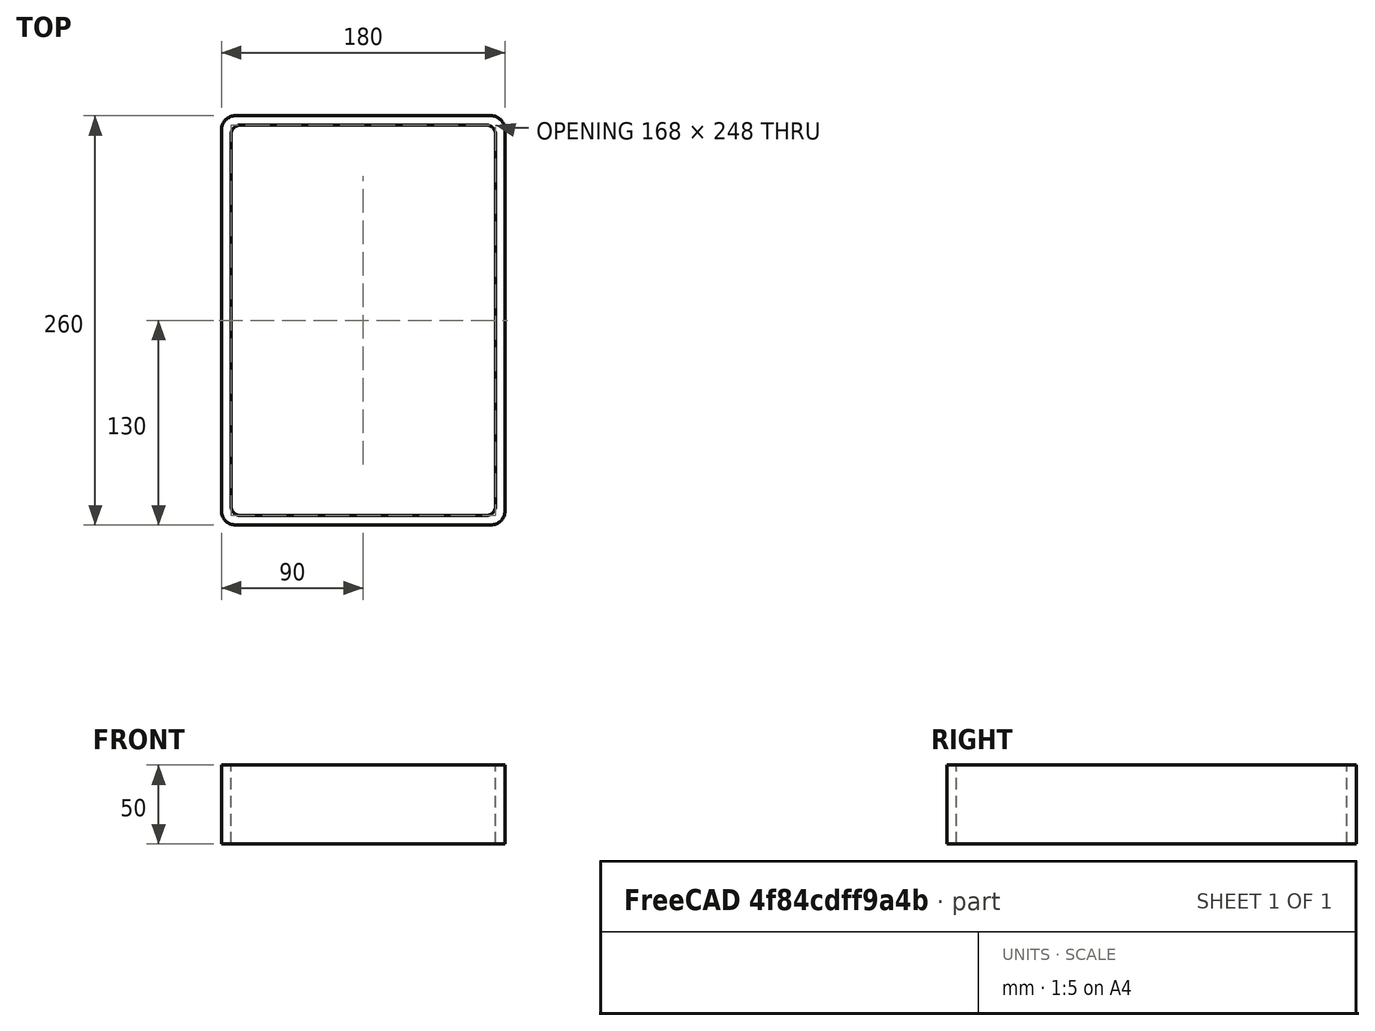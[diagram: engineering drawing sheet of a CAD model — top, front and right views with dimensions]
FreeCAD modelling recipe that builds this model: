
FCSTD DOCUMENT  (FreeCAD 0.15R4671 (Git))
Label: Rectangular hollow section 260x180x6 EN10219 S235JRH
License: All rights reserved
LicenseURL: http://en.wikipedia.org/wiki/All_rights_reserved
objects: Sketcher::SketchObject×1, Part::Extrusion×1
note: 2 computed .brp shape members not serialized (recipe doc carries the construction recipe); baked Part::Feature solids carry a one-line shape summary decoded from their .brp

FEATURE [Sketcher::SketchObject] Sketch
  sketch-geometry (16):
    g0: LineSegment StartX=-78 StartY=124 StartZ=0 EndX=78 EndY=124 EndZ=0
    g1: LineSegment StartX=84 StartY=118 StartZ=0 EndX=84 EndY=-118 EndZ=0
    g2: LineSegment StartX=78 StartY=-124 StartZ=0 EndX=-78 EndY=-124 EndZ=0
    g3: LineSegment StartX=-84 StartY=-118 StartZ=0 EndX=-84 EndY=118 EndZ=0
    g4: LineSegment StartX=-81 StartY=130 StartZ=0 EndX=81 EndY=130 EndZ=0
    g5: LineSegment StartX=90 StartY=121 StartZ=0 EndX=90 EndY=-121 EndZ=0
    g6: LineSegment StartX=81 StartY=-130 StartZ=0 EndX=-81 EndY=-130 EndZ=0
    g7: LineSegment StartX=-90 StartY=-121 StartZ=0 EndX=-90 EndY=121 EndZ=0
    g8: ArcOfCircle CenterX=-78 CenterY=118 CenterZ=0 NormalX=0 NormalY=0 NormalZ=1 Radius=6 StartAngle=1.5708 EndAngle=3.14159
    g9: ArcOfCircle CenterX=78 CenterY=118 CenterZ=0 NormalX=0 NormalY=0 NormalZ=1 Radius=6 StartAngle=0 EndAngle=1.5708
    g10: ArcOfCircle CenterX=78 CenterY=-118 CenterZ=0 NormalX=0 NormalY=0 NormalZ=1 Radius=6 StartAngle=4.71239 EndAngle=6.28319
    g11: ArcOfCircle CenterX=-78 CenterY=-118 CenterZ=0 NormalX=0 NormalY=0 NormalZ=1 Radius=6 StartAngle=3.14159 EndAngle=4.71239
    g12: ArcOfCircle CenterX=81 CenterY=121 CenterZ=0 NormalX=0 NormalY=0 NormalZ=1 Radius=9 StartAngle=0 EndAngle=1.5708
    g13: ArcOfCircle CenterX=81 CenterY=-121 CenterZ=0 NormalX=0 NormalY=0 NormalZ=1 Radius=9 StartAngle=4.71239 EndAngle=6.28319
    g14: ArcOfCircle CenterX=-81 CenterY=-121 CenterZ=0 NormalX=0 NormalY=0 NormalZ=1 Radius=9 StartAngle=3.14159 EndAngle=4.71239
    g15: ArcOfCircle CenterX=-81 CenterY=121 CenterZ=0 NormalX=0 NormalY=0 NormalZ=1 Radius=9 StartAngle=1.5708 EndAngle=3.14159
  constraints (36):
    c: Horizontal(g2)
    c: Vertical(g3)
    c: Horizontal(g6)
    c: Vertical(g7)
    c: Tangent(g3,g8) = 1.5708
    c: Tangent(g0,g8) = 1.5708
    c: Tangent(g0,g9) = 1.5708
    c: Tangent(g1,g9) = 1.5708
    c: Tangent(g1,g10) = 1.5708
    c: Tangent(g2,g10) = 1.5708
    c: Tangent(g2,g11) = 1.5708
    c: Tangent(g3,g11) = 1.5708
    c: Tangent(g4,g12) = 1.5708
    c: Tangent(g5,g12) = 1.5708
    c: Tangent(g5,g13) = 1.5708
    c: Tangent(g6,g13) = 1.5708
    c: Tangent(g6,g14) = 1.5708
    c: Tangent(g7,g14) = 1.5708
    c: Tangent(g7,g15) = 1.5708
    c: Tangent(g4,g15) = 1.5708
    c: Equal(g9,g8)
    c: Equal(g9,g11)
    c: Equal(g9,g10)
    c: Equal(g12,g15)
    c: Equal(g12,g14)
    c: Equal(g12,g13)
    c: Symmetric(g4,g6,g-1)
    c: Symmetric(g7,g5,g-2)
    c: DistanceY(g4,g6) = -260
    c: DistanceX(g7,g5) = 180
    c: Symmetric(g3,g1,g-2)
    c: Symmetric(g0,g2,g-1)
    c: DistanceY(g0,g4) = 6
    c: DistanceX(g5,g1) = -6
    c: Radius(g9) = 6
    c: Radius(g12) = 9
FEATURE [Part::Extrusion] Extrude  label="Rectangular hollow section 260x180x6 EN10219 S235JRH"
  Base = -> Sketch
  Dir = (0,0,50)
  Solid = true
